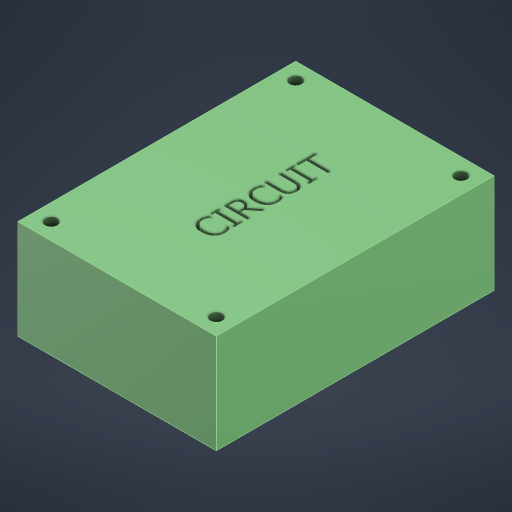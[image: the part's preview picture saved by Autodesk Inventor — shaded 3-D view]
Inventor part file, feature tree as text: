
AUTODESK INVENTOR PART (.ipt)
format: ipt  version: 2024.3 (Build 283343000, 343)  size: 382,464 bytes
history: native  units: mm
features: extrude x3, other x1, sketch x1, projected_geometry x1
ambient origin geometry x8: Origin, YZ Plane, XZ Plane, XY Plane, X Axis, Y Axis, Z Axis, Center Point
bodies: Body1 (feature_tree)
feature tree (6):
  other  "솔리드1"
  extrude  "돌출1"  Depth=50.0mm
  extrude  "돌출3"  Depth=70.0mm
  extrude  "돌출4"  Depth=25.0mm TaperAngle=0.0deg
  sketch  "스케치3"
  projected_geometry  "투영된 루프1"
